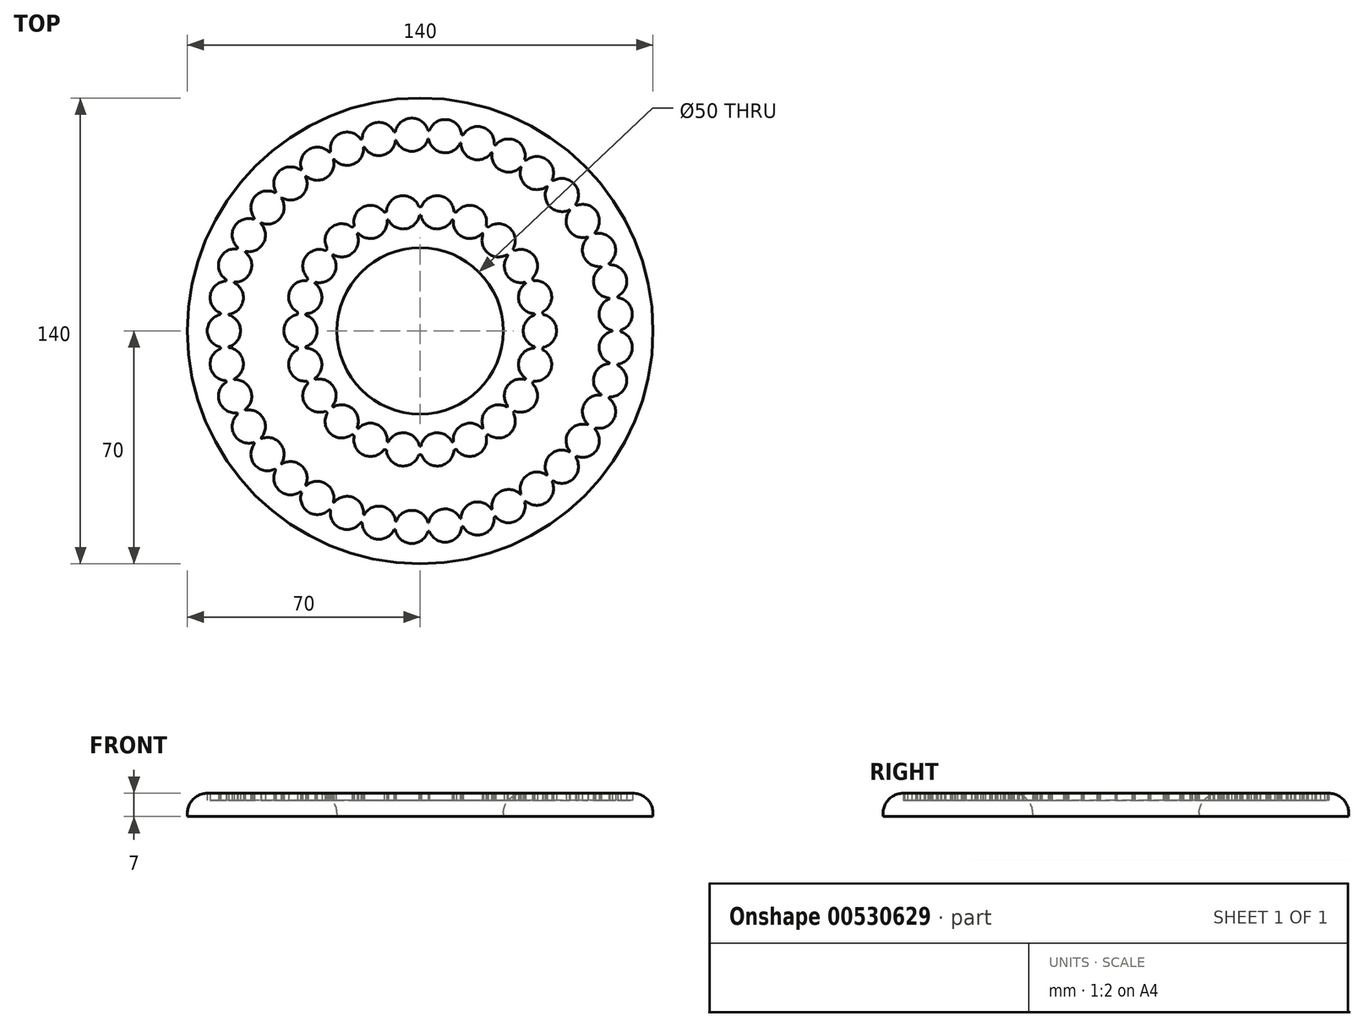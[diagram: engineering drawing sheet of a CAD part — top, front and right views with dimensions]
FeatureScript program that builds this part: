
annotation { "Feature Type Name" : "Feature", "Feature Type Description" : "" }
export const myFeature = defineFeature(function(context is Context, id is Id, definition is map)
    precondition{}
    {
        {
            var Q0;
            Q0=qCreatedBy(makeId("Front.planeOp"),FACE);
            var sketch = newSketch(context, id + "F0", { "sketchPlane" : qUnion([Q0])});
            skLineSegment(sketch, "E0", {"start": v(-70, 7) * mm, "end": v(-70, 0) * mm});
            skLineSegment(sketch, "E1", {"start": v(-70, 0) * mm, "end": v(-25, 0) * mm});
            skLineSegment(sketch, "E2", {"start": v(-25, 0) * mm, "end": v(-25, 7) * mm});
            skLineSegment(sketch, "E3", {"start": v(-25, 7) * mm, "end": v(-31, 7) * mm});
            skLineSegment(sketch, "E4", {"start": v(-31, 7) * mm, "end": v(-31, 4.9) * mm});
            skLineSegment(sketch, "E5", {"start": v(-31, 4.9) * mm, "end": v(-41, 4.9) * mm});
            skLineSegment(sketch, "E6", {"start": v(-41, 4.9) * mm, "end": v(-41, 7) * mm});
            skLineSegment(sketch, "E7", {"start": v(-41, 7) * mm, "end": v(-54, 7) * mm});
            skLineSegment(sketch, "E8", {"start": v(-54, 7) * mm, "end": v(-54, 4.9) * mm});
            skLineSegment(sketch, "E9", {"start": v(-54, 4.9) * mm, "end": v(-64, 4.9) * mm});
            skLineSegment(sketch, "E10", {"start": v(-64, 4.9) * mm, "end": v(-64, 7) * mm});
            skLineSegment(sketch, "E11", {"start": v(-64, 7) * mm, "end": v(-70, 7) * mm});
            skLineSegment(sketch, "E12", {"start": v(-35.5, 4.9) * mm, "end": v(-35.5, 0) * mm});
            skLineSegment(sketch, "E13", {"start": v(-36.5, 4.9) * mm, "end": v(-36.5, 0) * mm});
            skLineSegment(sketch, "E14", {"start": v(-58.5, 4.9) * mm, "end": v(-58.5, 0) * mm});
            skLineSegment(sketch, "E15", {"start": v(-59.5, 4.9) * mm, "end": v(-59.5, 0) * mm});
            skLineSegment(sketch, "E16", {"start": v(0, 0) * mm, "end": v(0, 30.11) * mm});
            skLineSegment(sketch, "E17", {"start": v(-64, 7) * mm, "end": v(-31, 7) * mm});
            skLineSegment(sketch, "E18", {"start": v(-59, 4.9) * mm, "end": v(-59, 7) * mm});
            skLineSegment(sketch, "E19", {"start": v(-36, 4.9) * mm, "end": v(-36, 7) * mm});
            skLineSegment(sketch, "E20", {"start": v(-60.25, 7) * mm, "end": v(-60.25, 4.9) * mm});
            skLineSegment(sketch, "E21", {"start": v(-57.75, 7) * mm, "end": v(-57.75, 4.9) * mm});
            skLineSegment(sketch, "E22", {"start": v(-37.25, 7) * mm, "end": v(-37.25, 4.9) * mm});
            skLineSegment(sketch, "E23", {"start": v(-34.75, 7) * mm, "end": v(-34.75, 4.9) * mm});
            skSolve(sketch);
        }
        {
            var Q0;
            {var subQ1=sQuery(id+"F0.wireOp",EDGE,"E2");Q0=makeQuery(id+"F0.imprint","IMPRINT",FACE,{"disambiguationData":[TD([[makeQuery(id+"F0.imprint","IMPRINT",EDGE,{"derivedFrom":subQ1}),1.0]])]});}
            var Q1;
            {var subQ0=sQuery(id+"F0.wireOp",EDGE,"E14");Q1=makeQuery(id+"F0.imprint","IMPRINT",FACE,{"disambiguationData":[TD([[makeQuery(id+"F0.imprint","IMPRINT",EDGE,{"derivedFrom":subQ0}),-1.0]])]});}
            var Q2;
            {var subQ4=sQuery(id+"F0.wireOp",EDGE,"E0");Q2=makeQuery(id+"F0.imprint","IMPRINT",FACE,{"disambiguationData":[TD([[makeQuery(id+"F0.imprint","IMPRINT",EDGE,{"derivedFrom":subQ4}),1.0]])]});}
            var Q3;
            {var subQ0=sQuery(id+"F0.wireOp",EDGE,"E6");Q3=makeQuery(id+"F0.imprint","IMPRINT",FACE,{"disambiguationData":[TD([[makeQuery(id+"F0.imprint","IMPRINT",EDGE,{"derivedFrom":subQ0}),1.0]])]});}
            var Q4;
            {var subQ0=sQuery(id+"F0.wireOp",EDGE,"E12");Q4=makeQuery(id+"F0.imprint","IMPRINT",FACE,{"disambiguationData":[TD([[makeQuery(id+"F0.imprint","IMPRINT",EDGE,{"derivedFrom":subQ0}),-1.0]])]});}
            var Q5;
            {var subQ4=sQuery(id+"F0.wireOp",EDGE,"E8");Q5=makeQuery(id+"F0.imprint","IMPRINT",FACE,{"disambiguationData":[TD([[makeQuery(id+"F0.imprint","IMPRINT",EDGE,{"derivedFrom":subQ4}),-1.0]])]});}
            var Q6;
            {var subQ4=sQuery(id+"F0.wireOp",EDGE,"E4");Q6=makeQuery(id+"F0.imprint","IMPRINT",FACE,{"disambiguationData":[TD([[makeQuery(id+"F0.imprint","IMPRINT",EDGE,{"derivedFrom":subQ4}),-1.0]])]});}
            var Q7;
            {var subQ1=sQuery(id+"F0.wireOp",EDGE,"E10");Q7=makeQuery(id+"F0.imprint","IMPRINT",FACE,{"disambiguationData":[TD([[makeQuery(id+"F0.imprint","IMPRINT",EDGE,{"derivedFrom":subQ1}),-1.0]])]});}
            var Q8;
            {var subQ0=sQuery(id+"F0.wireOp",EDGE,"E6");Q8=makeQuery(id+"F0.imprint","IMPRINT",FACE,{"disambiguationData":[TD([[makeQuery(id+"F0.imprint","IMPRINT",EDGE,{"derivedFrom":subQ0}),-1.0]])]});}
            var Q9;
            Q9=sQuery(id+"F0.wireOp",EDGE,"E7");
            var Q10;
            Q10=sQuery(id+"F0.wireOp",EDGE,"E1");
            var Q11;
            Q11=sQuery(id+"F0.wireOp",EDGE,"E8");
            var Q12;
            Q12=sQuery(id+"F0.wireOp",EDGE,"E6");
            var Q13;
            Q13=sQuery(id+"F0.wireOp",EDGE,"E5");
            var Q14;
            Q14=sQuery(id+"F0.wireOp",EDGE,"E12");
            var Q15;
            Q15=sQuery(id+"F0.wireOp",EDGE,"E4");
            var Q16;
            Q16=sQuery(id+"F0.wireOp",EDGE,"E9");
            var Q17;
            Q17=sQuery(id+"F0.wireOp",EDGE,"E10");
            var Q18;
            Q18=sQuery(id+"F0.wireOp",EDGE,"E2");
            var Q19;
            Q19=sQuery(id+"F0.wireOp",EDGE,"E3");
            var Q20;
            Q20=sQuery(id+"F0.wireOp",EDGE,"E14");
            var Q21;
            Q21=sQuery(id+"F0.wireOp",EDGE,"E15");
            var Q22;
            Q22=sQuery(id+"F0.wireOp",EDGE,"E0");
            var Q23;
            Q23=sQuery(id+"F0.wireOp",EDGE,"E13");
            var Q24;
            Q24=sQuery(id+"F0.wireOp",EDGE,"E11");
            var Q25;
            Q25=sQuery(id+"F0.wireOp",EDGE,"E16");
            revolve(context, id + "F1", {"entities" : qUnion([Q0, Q1, Q2, Q3, Q4, Q5, Q6, Q7, Q8]), "surfaceEntities" : qUnion([Q9, Q10, Q11, Q12, Q13, Q14, Q15, Q16, Q17, Q18, Q19, Q20, Q21, Q22, Q23, Q24]), "axis" : qUnion([Q25]), "revolveType" : RevolveType.FULL});
        }
        {
            var Q0;
            {var subQ1=sQuery(id+"F0.wireOp",EDGE,"E10");Q0=makeQuery(id+"F0.imprint","IMPRINT",FACE,{"disambiguationData":[TD([[makeQuery(id+"F0.imprint","IMPRINT",EDGE,{"derivedFrom":subQ1}),-1.0]])]});}
            var Q1;
            Q1=sQuery(id+"F0.wireOp",EDGE,"E18");
            revolve(context, id + "F2", {"entities" : qUnion([Q0]), "axis" : qUnion([Q1]), "revolveType" : RevolveType.FULL});
        }
        {
            var Q0;
            Q0=makeQuery(id+"F2.opRevolve","SWEPT_BODY",BODY,{"disambiguationData":[OSD([sQuery(id+"F0.wireOp",EDGE,"E9"),sQuery(id+"F0.wireOp",EDGE,"E10"),sQuery(id+"F0.wireOp",EDGE,"E17"),sQuery(id+"F0.wireOp",EDGE,"E18")])]});
            var Q1;
            Q1=sQuery(id+"F0.wireOp",EDGE,"E16");
            circularPattern(context, id + "F3", {"operationType" : NewBodyOperationType.REMOVE, "entities" : qUnion([Q0]), "axis" : qUnion([Q1]), "angle" : 360 * degree, "instanceCount" : 37, "equalSpace" : true});
        }
        {
            var Q0;
            {var subQ0=sQuery(id+"F0.wireOp",EDGE,"E6");Q0=makeQuery(id+"F0.imprint","IMPRINT",FACE,{"disambiguationData":[TD([[makeQuery(id+"F0.imprint","IMPRINT",EDGE,{"derivedFrom":subQ0}),-1.0]])]});}
            var Q1;
            Q1=sQuery(id+"F0.wireOp",EDGE,"E19");
            revolve(context, id + "F4", {"entities" : qUnion([Q0]), "axis" : qUnion([Q1]), "revolveType" : RevolveType.FULL});
        }
        {
            var Q0;
            Q0=makeQuery(id+"F4.opRevolve","SWEPT_BODY",BODY,{"disambiguationData":[OSD([sQuery(id+"F0.wireOp",EDGE,"E5"),sQuery(id+"F0.wireOp",EDGE,"E6"),sQuery(id+"F0.wireOp",EDGE,"E17"),sQuery(id+"F0.wireOp",EDGE,"E19")])]});
            var Q1;
            Q1=sQuery(id+"F0.wireOp",EDGE,"E16");
            circularPattern(context, id + "F5", {"operationType" : NewBodyOperationType.REMOVE, "entities" : qUnion([Q0]), "axis" : qUnion([Q1]), "angle" : 360 * degree, "instanceCount" : 22, "equalSpace" : true});
        }
        {
            var Q0;
            Q0=makeQuery(id+"F1.opRevolve","SWEPT_EDGE",EDGE,{"disambiguationData":[OSD([sQuery(id+"F0.wireOp",EDGE,"E0"),sQuery(id+"F0.wireOp",EDGE,"E11")])]});
            var Q1;
            Q1=makeQuery(id+"F1.opRevolve","SWEPT_EDGE",EDGE,{"disambiguationData":[OSD([sQuery(id+"F0.wireOp",EDGE,"E2"),sQuery(id+"F0.wireOp",EDGE,"E3")])]});
            fillet(context, id + "F6", {"entities" : qUnion([Q0, Q1]), "radius" : 6 * mm, "tangentPropagation" : true, "allowEdgeOverflow" : false});
        }
    });
